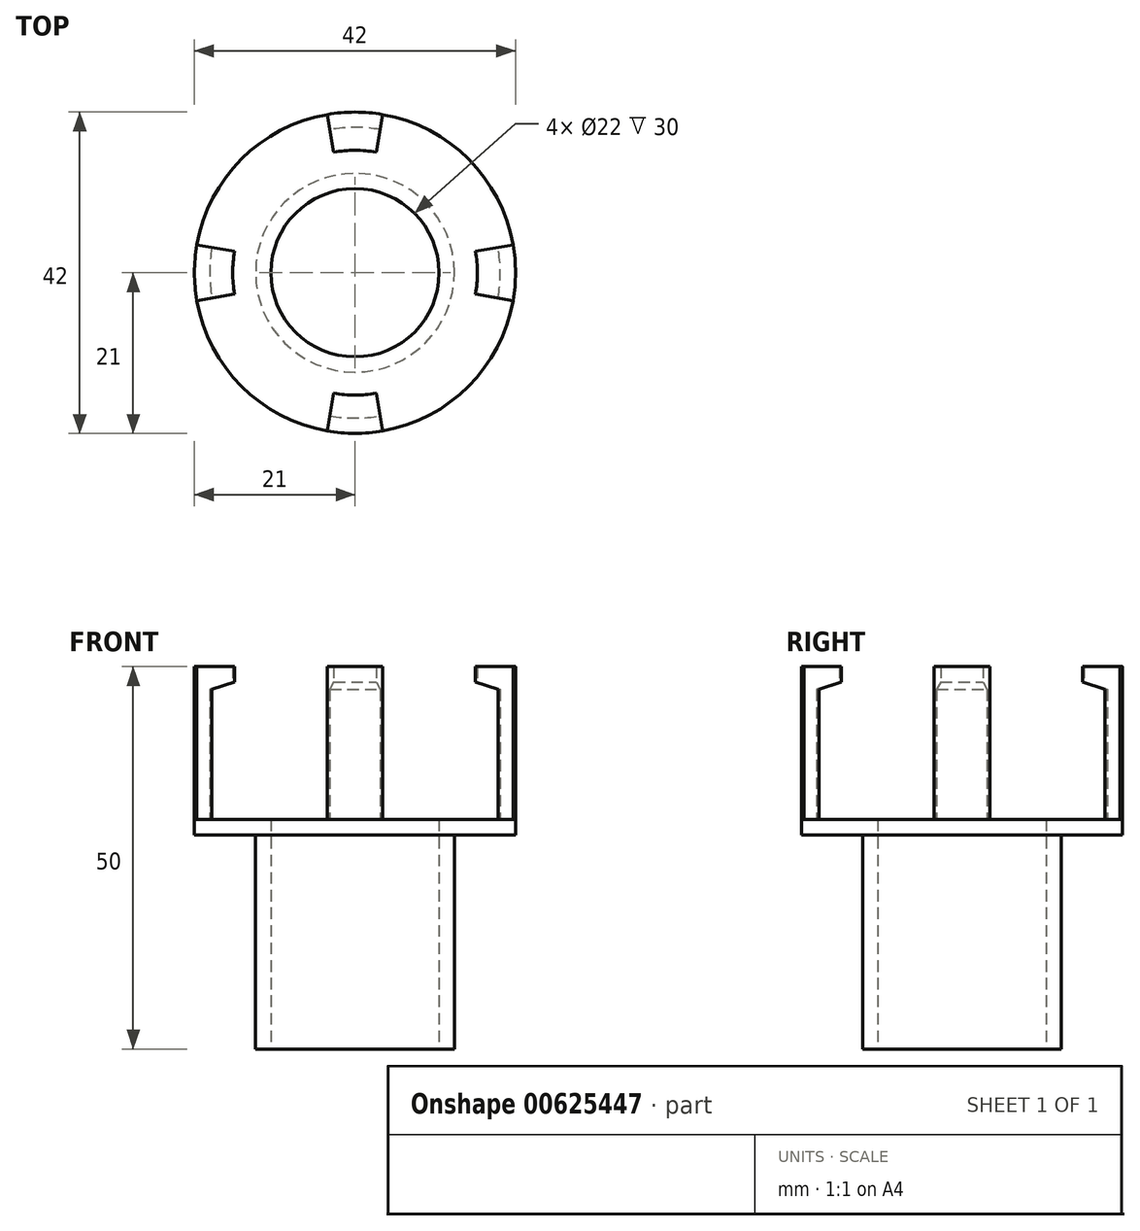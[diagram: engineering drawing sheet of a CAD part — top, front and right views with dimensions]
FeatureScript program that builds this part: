
annotation { "Feature Type Name" : "Feature", "Feature Type Description" : "" }
export const myFeature = defineFeature(function(context is Context, id is Id, definition is map)
    precondition{}
    {
        {
            var Q0;
            Q0=qCreatedBy(makeId("Front.planeOp"),FACE);
            var sketch = newSketch(context, id + "F0", { "sketchPlane" : qUnion([Q0])});
            skLineSegment(sketch, "E0", {"start": v(11, 0) * mm, "end": v(11, 30) * mm});
            skLineSegment(sketch, "E1", {"start": v(13, 0) * mm, "end": v(13, 28) * mm});
            skLineSegment(sketch, "E2", {"start": v(11, 30) * mm, "end": v(21, 30) * mm});
            skLineSegment(sketch, "E3", {"start": v(13, 28) * mm, "end": v(21, 28) * mm});
            skLineSegment(sketch, "E4", {"start": v(0, -7.2) * mm, "end": v(0, 71.9) * mm, "construction": true});
            skLineSegment(sketch, "E5", {"start": v(11, 0) * mm, "end": v(13, 0) * mm});
            skLineSegment(sketch, "E6", {"start": v(21, 30) * mm, "end": v(21, 28) * mm});
            skSolve(sketch);
        }
        {
            var Q0;
            Q0=qSketchRegion(id+"F0",true);
            var Q1;
            Q1=sQuery(id+"F0.wireOp",EDGE,"E4");
            revolve(context, id + "F1", {"entities" : qUnion([Q0]), "axis" : qUnion([Q1]), "revolveType" : RevolveType.FULL});
        }
        {
            var Q0;
            Q0=qCreatedBy(makeId("Front.planeOp"),FACE);
            var sketch = newSketch(context, id + "F2", { "sketchPlane" : qUnion([Q0])});
            skLineSegment(sketch, "E7", {"start": v(21, 30) * mm, "end": v(21, 50) * mm});
            skLineSegment(sketch, "E8", {"start": v(21, 50) * mm, "end": v(16, 50) * mm});
            skLineSegment(sketch, "E9", {"start": v(16, 50) * mm, "end": v(16, 48) * mm});
            skLineSegment(sketch, "E10", {"start": v(16, 48) * mm, "end": v(19, 47) * mm});
            skLineSegment(sketch, "E11", {"start": v(19, 47) * mm, "end": v(19, 30) * mm});
            skLineSegment(sketch, "E12", {"start": v(19, 30) * mm, "end": v(21, 30) * mm});
            skLineSegment(sketch, "E13", {"start": v(0, 0) * mm, "end": v(58.12, 0) * mm, "construction": true});
            skSolve(sketch);
        }
        {
            var Q0;
            Q0=makeQuery(id+"F2.imprint","IMPRINT",FACE,{"disambiguationData":[TD([[makeQuery(id+"F2.imprint","IMPRINT",EDGE,{"derivedFrom":sQuery(id+"F2.wireOp",EDGE,"E7")}),1.0]])]});
            var Q1;
            Q1=sQuery(id+"F0.wireOp",EDGE,"E4");
            revolve(context, id + "F3", {"operationType" : NewBodyOperationType.ADD, "entities" : qUnion([Q0]), "axis" : qUnion([Q1]), "revolveType" : RevolveType.SYMMETRIC, "angle" : 20 * degree});
        }
        {
            var Q0;
            Q0=makeQuery(id+"F1.opRevolve","SWEPT_BODY",BODY,{"disambiguationData":[OSD([sQuery(id+"F0.wireOp",EDGE,"E0"),sQuery(id+"F0.wireOp",EDGE,"E1"),sQuery(id+"F0.wireOp",EDGE,"E2"),sQuery(id+"F0.wireOp",EDGE,"E3"),sQuery(id+"F0.wireOp",EDGE,"E5"),sQuery(id+"F0.wireOp",EDGE,"E6")])]});
            var Q1;
            Q1=sQuery(id+"F0.wireOp",EDGE,"E4");
            circularPattern(context, id + "F4", {"entities" : qUnion([Q0]), "axis" : qUnion([Q1]), "angle" : 360 * degree, "instanceCount" : 4, "equalSpace" : true});
        }
    });
